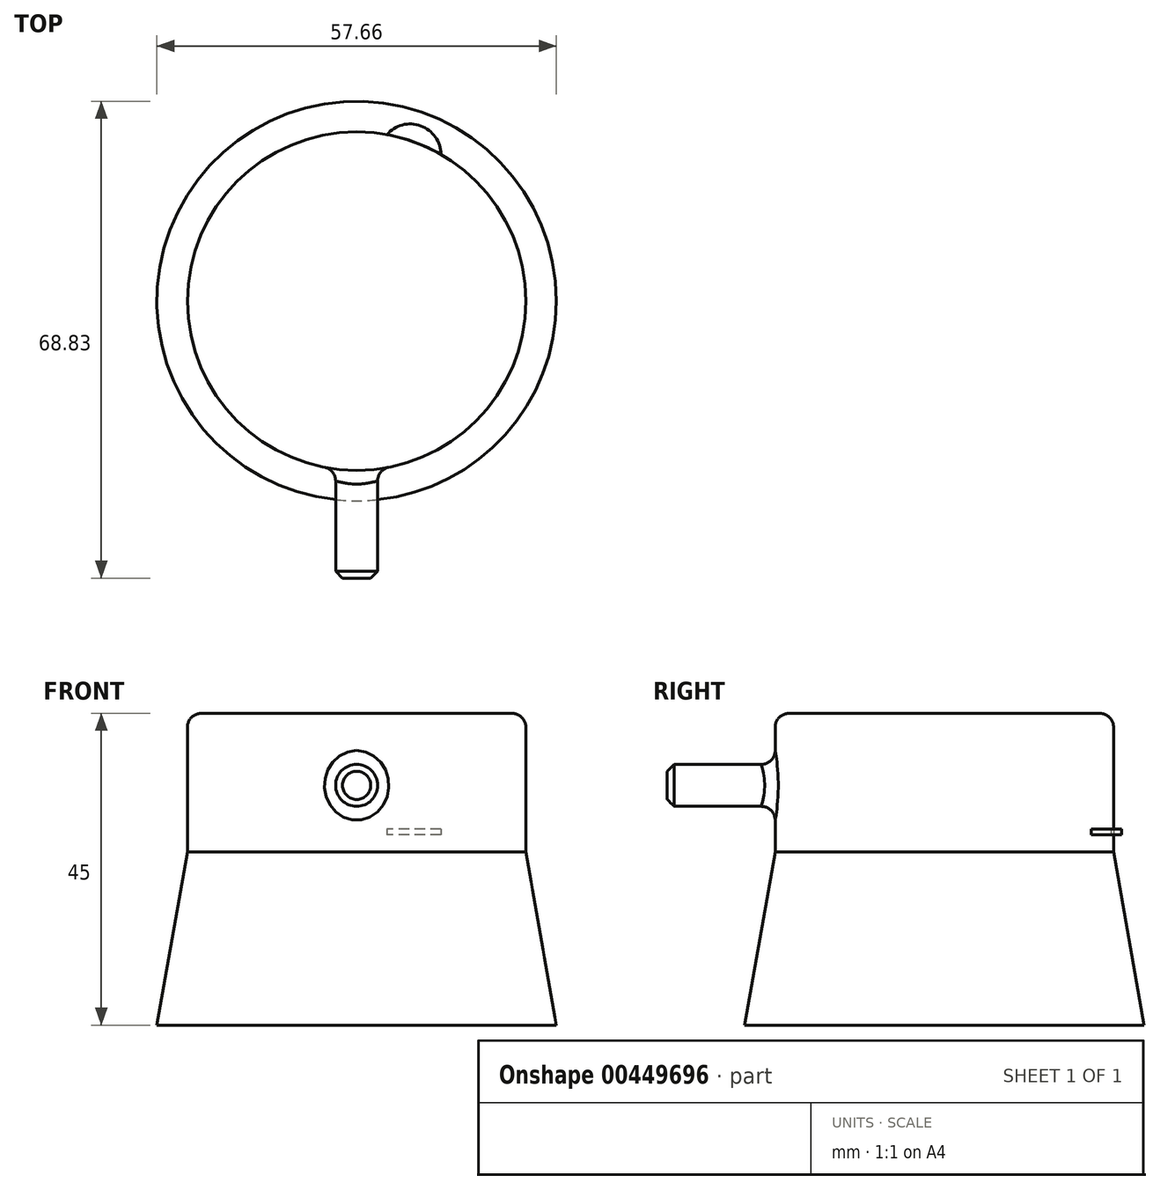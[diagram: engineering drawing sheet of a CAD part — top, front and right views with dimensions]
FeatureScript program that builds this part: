
annotation { "Feature Type Name" : "Feature", "Feature Type Description" : "" }
export const myFeature = defineFeature(function(context is Context, id is Id, definition is map)
    precondition{}
    {
        {
            var Q0;
            Q0=qCreatedBy(makeId("Top.planeOp"),FACE);
            var sketch = newSketch(context, id + "F0", { "sketchPlane" : qUnion([Q0])});
            skCircle(sketch, "E0", {"center": v(0, 0) * mm, "radius": 24.42 * mm});
            skSolve(sketch);
        }
        {
            var Q0;
            Q0=makeQuery(id+"F0.imprint","IMPRINT",FACE,{"disambiguationData":[TD([[makeQuery(id+"F0.imprint","IMPRINT",EDGE,{"derivedFrom":sQuery(id+"F0.wireOp",EDGE,"E0")}),1.0]])]});
            extrude(context, id + "F1", {"entities" : qUnion([Q0]), "depth" : 20 * mm});
        }
        {
            var Q0;
            Q0=qCreatedBy(makeId("Top.planeOp"),FACE);
            var sketch = newSketch(context, id + "F2", { "sketchPlane" : qUnion([Q0])});
            skCircle(sketch, "E1.0", {"center": v(0, 0) * mm, "radius": 24.42 * mm});
            skArc(sketch, "E2", {"start": v(12.18, 21.17) * mm, "mid": v(9.25, 25.3) * mm, "end": v(4.35, 24.03) * mm});
            skSolve(sketch);
        }
        {
            var Q0;
            Q0=qCreatedBy(makeId("Top.planeOp"),FACE);
            cPlane(context, id + "F3", {"entities" : qUnion([Q0]), "cplaneType" : CPlaneType.OFFSET, "offset" : 2.5 * mm, "width" : 150 * mm, "height" : 150 * mm});
        }
        {
            var Q0;
            Q0=qCreatedBy(id+"F3.planeOp",FACE);
            var sketch = newSketch(context, id + "F4", { "sketchPlane" : qUnion([Q0])});
            skArc(sketch, "E3.0", {"start": v(12.18, 21.17) * mm, "mid": v(9.25, 25.3) * mm, "end": v(4.35, 24.03) * mm});
            skArc(sketch, "E4.0", {"start": v(12.18, 21.17) * mm, "mid": v(8.39, 22.93) * mm, "end": v(4.35, 24.03) * mm});
            skSolve(sketch);
        }
        {
            var Q0;
            Q0 = qSketchRegion(id + "F4", true);
            extrude(context, id + "F5", {"entities" : qUnion([Q0]), "operationType" : NewBodyOperationType.ADD, "depth" : 0.8 * mm});
        }
        {
            var Q0;
            Q0=qCreatedBy(makeId("Front.planeOp"),FACE);
            var sketch = newSketch(context, id + "F6", { "sketchPlane" : qUnion([Q0])});
            skCircle(sketch, "E5", {"center": v(0, 9.6) * mm, "radius": 3.03 * mm});
            skSolve(sketch);
        }
        {
            var Q0;
            Q0 = qSketchRegion(id + "F6", true);
            extrude(context, id + "F7", {"entities" : qUnion([Q0]), "operationType" : NewBodyOperationType.ADD, "depth" : 40 * mm});
        }
        {
            var Q0;
            Q0=makeQuery(id+"F1.opExtrude","CAP_EDGE",EDGE,{"disambiguationData":[OSD([sQuery(id+"F0.wireOp",EDGE,"E0")])],"isStart":false});
            var Q1;
            Q1=makeQuery(id+"F7.boolean.opBoolean","INTERSECT",EDGE,{"derivedFrom":[makeQuery(id+"F1.opExtrude","SWEPT_FACE",FACE,{"disambiguationData":[OSD([sQuery(id+"F0.wireOp",EDGE,"E0")])]}),makeQuery(id+"F7.opExtrude","SWEPT_FACE",FACE,{"disambiguationData":[OSD([sQuery(id+"F6.wireOp",EDGE,"E5")])]})]});
            fillet(context, id + "F8", {"entities" : qUnion([Q0, Q1]), "radius" : 2 * mm, "tangentPropagation" : true, "allowEdgeOverflow" : false});
        }
        {
            var Q0;
            Q0=makeQuery(id+"F7.opExtrude","CAP_EDGE",EDGE,{"disambiguationData":[OSD([sQuery(id+"F6.wireOp",EDGE,"E5")])],"isStart":false});
            chamfer(context, id + "F9", {"entities" : qUnion([Q0]), "width" : 1 * mm, "tangentPropagation" : true});
        }
        {
            var Q0;
            {var subQ0=sQuery(id+"F2.wireOp",EDGE,"E2");var subQ1=sQuery(id+"F2.wireOp",EDGE,"E1.0");var subQ2=makeQuery(id+"F2.imprint","INTERSECT",VERTEX,{"disambiguationData":[OD(0.0)],"derivedFrom":[subQ1,subQ0]});Q0=makeQuery(id+"F2.imprint","IMPRINT",FACE,{"disambiguationData":[TD([[makeQuery(id+"F2.imprint","IMPRINT",EDGE,{"disambiguationData":[TD([[subQ2,-1.0]])],"derivedFrom":subQ1}),1.0]])]});}
            extrude(context, id + "F10", {"entities" : qUnion([Q0]), "operationType" : NewBodyOperationType.ADD, "oppositeDirection" : true, "depth" : 25 * mm, "hasDraft" : true, "draftAngle" : 10 * degree});
        }
    });
